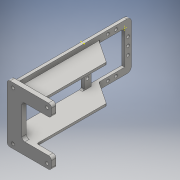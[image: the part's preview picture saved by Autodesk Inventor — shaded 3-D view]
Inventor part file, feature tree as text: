
AUTODESK INVENTOR PART (.ipt)
format: ipt  version: 2016 (Build 200138000, 138)  size: 299,008 bytes
history: native  units: mm
features: sketch x18, hole x12, fillet x10, extrude x8
ambient origin geometry x8: Origin, YZ Plane, XZ Plane, XY Plane, X Axis, Y Axis, Z Axis, Center Point
bodies: 实体1 (feature_tree)
feature tree (48):
  sketch  "草图1"  dims[d0=32.0mm d1=32.0mm]
  extrude  "拉伸1"  Depth=32.0mm
  sketch  "草图3"  dims[d4=2.0mm d5=0.0mm]
  hole  "孔1"  [1 undecoded]
  sketch  "草图4"  dims[d6=2.35mm d16=16.0mm d8=2.0mm d9=6.0mm d10=3.023mm d11=2.0mm d12=14.3117mm d13=8.0mm d14=20.594885mm]
  sketch  "草图5"  dims[d17=2.35mm d18=16.0mm d19=2.0mm d20=6.0mm d21=3.023mm d22=2.0mm d23=14.3117mm d24=8.0mm d25=20.594885mm]
  hole  "孔2"  [1 undecoded]
  hole  "孔3"  [1 undecoded]
  hole  "孔4"  [1 undecoded]
  hole  "孔5"  [1 undecoded]
  hole  "孔6"  [1 undecoded]
  hole  "孔7"  [1 undecoded]
  hole  "孔8"  [1 undecoded]
  hole  "孔9"  [1 undecoded]
  hole  "孔10"  [1 undecoded]
  hole  "孔11"  [1 undecoded]
  hole  "孔12"  [1 undecoded]
  extrude  "拉伸2"  Depth=2.0mm
  sketch  "草图7"  dims[d35=2.35mm d36=16.0mm d37=2.0mm d38=6.0mm d39=3.023mm d40=2.0mm d41=14.3117mm d42=8.0mm d43=20.594885mm]
  sketch  "草图8"  dims[d44=5.9mm d45=2.35mm d46=2.0mm d47=6.0mm d48=3.023mm d49=2.0mm d50=14.3117mm d51=8.0mm d52=20.594885mm]
  sketch  "草图9"  dims[d53=2.35mm d64=10.0mm d55=2.0mm d56=6.0mm d57=3.023mm d58=2.0mm d59=14.3117mm d60=8.0mm d61=20.594885mm]
  sketch  "草图10"  dims[d62=5.9mm d63=2.35mm d65=2.0mm d66=6.0mm d67=3.023mm d68=2.0mm d69=14.3117mm d70=8.0mm d71=20.594885mm d72=5.9mm d73=2.35mm]
  sketch  "草图11"  dims[d74=2.0mm d75=6.0mm d76=3.023mm d77=2.0mm d78=14.3117mm d79=8.0mm d80=20.594885mm d81=5.9mm d82=2.35mm]
  sketch  "草图12"  dims[d83=2.0mm d84=6.0mm d85=3.023mm d86=2.0mm d87=14.3117mm d88=8.0mm d89=20.594885mm d90=5.9mm d91=2.35mm]
  extrude  "拉伸3"  Depth=2.0mm
  extrude  "拉伸4"  Depth=2.0mm
  extrude  "拉伸5"  Depth=3.0mm TaperAngle=0.0deg
  extrude  "拉伸6"  Depth=3.0mm
  fillet  "圆角1"  Radius=3.0mm
  fillet  "圆角2"  Radius=3.0mm
  extrude  "拉伸7"  Depth=1.0mm
  extrude  "拉伸8"  Depth=3.0mm
  fillet  "圆角3"  Radius=4.0mm
  fillet  "圆角4"  Radius=3.0mm
  fillet  "圆角5"  Radius=2.0mm
  fillet  "圆角6"  Radius=2.0mm
  fillet  "圆角7"  Radius=3.0mm
  fillet  "圆角8"  Radius=1.0mm
  fillet  "圆角9"  Radius=1.0mm
  fillet  "圆角10"  Radius=1.0mm
  sketch  "草图17"  dims[d124=10.0mm d125=15.0mm]
  sketch  "草图18"  dims[d126=1.5mm d127=0.0mm d128=1.5mm d129=0.0mm d130=50.0mm d131=0.0mm d146=2.0mm d149=2.0mm d152=2.0mm d154=2.0mm d155=3.0mm d156=0.0mm d157=3.0mm d158=3.0mm d159=3.0mm d160=0.0mm d161=4.0mm d163=3.0mm d166=4.0mm d167=3.0mm d168=2.0mm d169=2.0mm d170=3.0mm d171=0.0mm d172=1.0mm d173=1.0mm d174=1.0mm d175=1.0mm d176=1.0mm d177=1.0mm d178=1.0mm d179=1.0mm d7=1.0mm]
  sketch  "草图2"  dims[d2=22.7mm d3=22.7mm]
  sketch  "草图6"  dims[d26=2.35mm d27=16.0mm d28=2.0mm d29=6.0mm d30=3.023mm d31=2.0mm d32=14.3117mm d33=8.0mm d34=20.594885mm]
  sketch  "草图13"  dims[d92=2.0mm d93=6.0mm d94=3.023mm d95=2.0mm d96=14.3117mm d97=8.0mm d98=20.594885mm d99=5.9mm d100=2.35mm]
  sketch  "草图14"  dims[d101=2.0mm d102=6.0mm d103=3.023mm d104=2.0mm d105=14.3117mm d106=8.0mm d107=20.594885mm d108=5.9mm d109=2.35mm]
  sketch  "草图15"  dims[d110=2.0mm d111=6.0mm d112=3.023mm d113=2.0mm d114=14.3117mm d115=8.0mm d116=20.594885mm d117=2.0mm d118=0.0mm]
  sketch  "草图16"  dims[d121=15.0mm d123=10.0mm]
note: 12 required parameter values undecoded (feature->parameter linkage not recoverable at this tier; creation-order binding heuristic only, values carry confidence <= 0.55)
